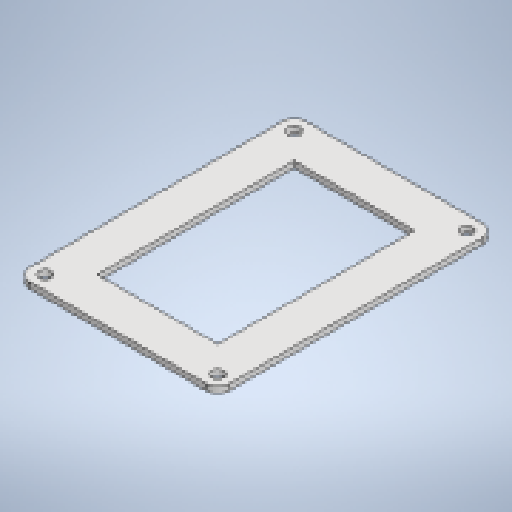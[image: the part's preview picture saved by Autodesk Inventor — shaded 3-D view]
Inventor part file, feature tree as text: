
AUTODESK INVENTOR PART (.ipt)
format: ipt  version: 2025.3 (Build 293356030, 356C)  size: 216,576 bytes
history: native  units: mm
features: other x3, sketch x2, sheet_metal_op x1, chamfer x1, projected_geometry x1
ambient origin geometry x8: Origin, YZ Plane, XZ Plane, XY Plane, X Axis, Y Axis, Z Axis, Center Point
bodies: Body1 (feature_tree)
feature tree (8):
  sheet_metal_op  "Face3"
  chamfer  "Corner Round1"
  sketch  "Sketch1"  dims[d156=3.0mm]
  other  "Plate5"
  sketch  "Sketch9"  dims[d172=60.0mm d174=6.0mm d176=3.0mm d177=0.0mm d178=6.0mm d180=20.0mm d181=20.0mm d182=98.0mm d183=7.0mm d184=7.0mm]
  projected_geometry  "Projected Loop3"
  other  "Cut2"
  other  "Definition1"
